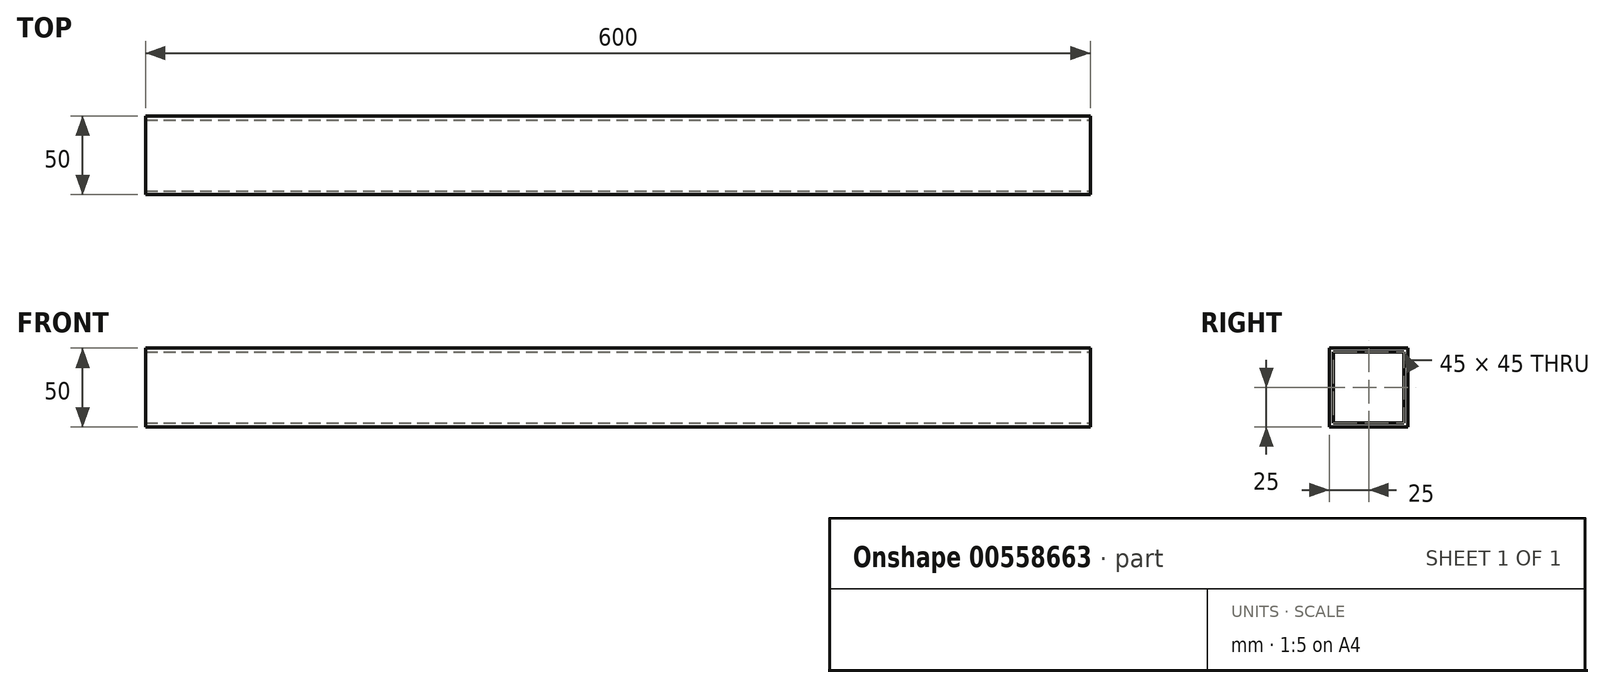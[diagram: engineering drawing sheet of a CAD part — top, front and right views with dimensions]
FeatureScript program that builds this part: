
annotation { "Feature Type Name" : "Feature", "Feature Type Description" : "" }
export const myFeature = defineFeature(function(context is Context, id is Id, definition is map)
    precondition{}
    {
        {
            var Q0;
            Q0=qCreatedBy(makeId("Right.planeOp"),FACE);
            var sketch = newSketch(context, id + "F0", { "sketchPlane" : qUnion([Q0])});
            skLineSegment(sketch, "E0.bottom", {"start": v(-25, -25) * mm, "end": v(25, -25) * mm});
            skLineSegment(sketch, "E0.top", {"start": v(-25, 25) * mm, "end": v(25, 25) * mm});
            skLineSegment(sketch, "E0.left", {"start": v(-25, -25) * mm, "end": v(-25, 25) * mm});
            skLineSegment(sketch, "E0.right", {"start": v(25, -25) * mm, "end": v(25, 25) * mm});
            skPoint(sketch, "E0.middle", {"position": v(0, 0) * mm});
            skLineSegment(sketch, "E1.bottom", {"start": v(-22.5, -22.5) * mm, "end": v(22.5, -22.5) * mm});
            skLineSegment(sketch, "E1.top", {"start": v(-22.5, 22.5) * mm, "end": v(22.5, 22.5) * mm});
            skLineSegment(sketch, "E1.left", {"start": v(-22.5, -22.5) * mm, "end": v(-22.5, 22.5) * mm});
            skLineSegment(sketch, "E1.right", {"start": v(22.5, -22.5) * mm, "end": v(22.5, 22.5) * mm});
            skSolve(sketch);
        }
        {
            var Q0;
            Q0=makeQuery(id+"F0.imprint","IMPRINT",FACE,{"disambiguationData":[TD([[makeQuery(id+"F0.imprint","IMPRINT",EDGE,{"derivedFrom":sQuery(id+"F0.wireOp",EDGE,"E0.bottom")}),1.0]])]});
            extrude(context, id + "F1", {"entities" : qUnion([Q0]), "oppositeDirection" : true, "depth" : 600 * mm, "offsetDistance" : 25 * mm});
        }
    });
